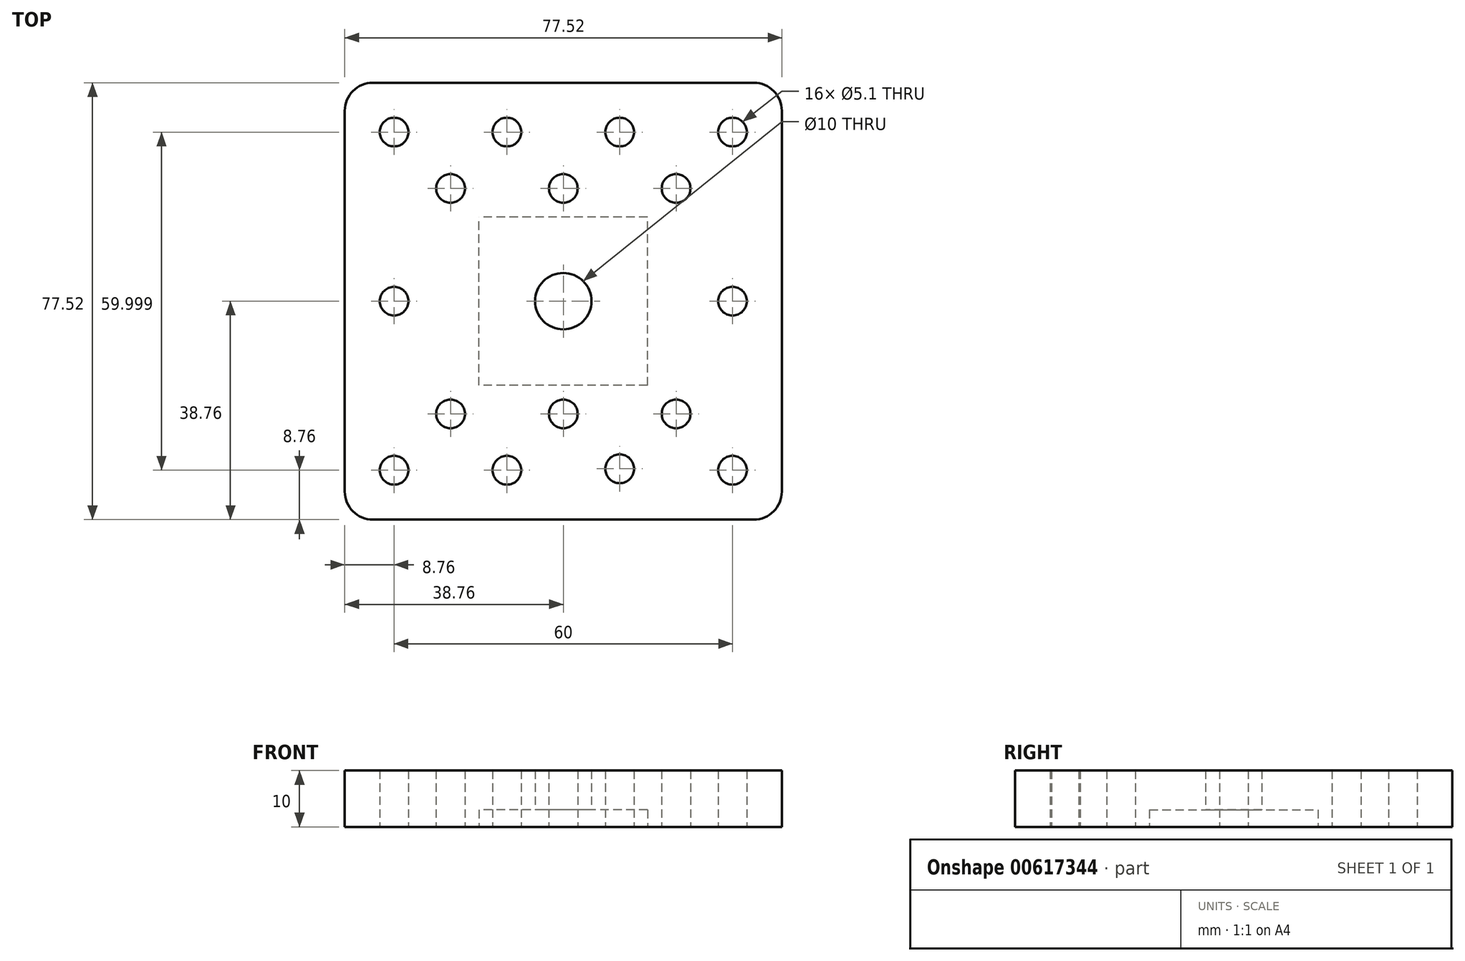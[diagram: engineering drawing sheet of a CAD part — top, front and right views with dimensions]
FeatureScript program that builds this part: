
annotation { "Feature Type Name" : "Feature", "Feature Type Description" : "" }
export const myFeature = defineFeature(function(context is Context, id is Id, definition is map)
    precondition{}
    {
        {
            var Q0;
            Q0=qCreatedBy(makeId("Top.planeOp"),FACE);
            var sketch = newSketch(context, id + "F0", { "sketchPlane" : qUnion([Q0])});
            skLineSegment(sketch, "E0.bottom", {"start": v(38.75, 38.76) * mm, "end": v(-38.76, 38.76) * mm});
            skLineSegment(sketch, "E0.top", {"start": v(38.76, -38.76) * mm, "end": v(-38.76, -38.76) * mm});
            skLineSegment(sketch, "E0.left", {"start": v(38.75, 38.76) * mm, "end": v(38.76, -38.76) * mm});
            skLineSegment(sketch, "E0.right", {"start": v(-38.76, 38.76) * mm, "end": v(-38.75, -38.76) * mm});
            skPoint(sketch, "E0.middle", {"position": v(0, 0) * mm});
            skLineSegment(sketch, "E1.bottom", {"start": v(14.95, -14.95) * mm, "end": v(-14.95, -14.95) * mm});
            skLineSegment(sketch, "E1.top", {"start": v(14.95, 14.95) * mm, "end": v(-14.95, 14.95) * mm});
            skLineSegment(sketch, "E1.left", {"start": v(14.95, -14.95) * mm, "end": v(14.95, 14.95) * mm});
            skLineSegment(sketch, "E1.right", {"start": v(-14.95, -14.95) * mm, "end": v(-14.95, 14.95) * mm});
            skCircle(sketch, "E2", {"center": v(-30, -30) * mm, "radius": 2.55 * mm});
            skCircle(sketch, "E3", {"center": v(-10, -30) * mm, "radius": 2.55 * mm});
            skCircle(sketch, "E4", {"center": v(10, -29.75) * mm, "radius": 2.55 * mm});
            skCircle(sketch, "E5", {"center": v(30, -30) * mm, "radius": 2.55 * mm});
            skCircle(sketch, "E6", {"center": v(20, -20) * mm, "radius": 2.55 * mm});
            skCircle(sketch, "E7", {"center": v(0, -20) * mm, "radius": 2.55 * mm});
            skCircle(sketch, "E8", {"center": v(-20, -20) * mm, "radius": 2.55 * mm});
            skCircle(sketch, "E9", {"center": v(-30, 30) * mm, "radius": 2.55 * mm});
            skCircle(sketch, "E10", {"center": v(-10, 30) * mm, "radius": 2.55 * mm});
            skCircle(sketch, "E11", {"center": v(10, 30) * mm, "radius": 2.55 * mm});
            skCircle(sketch, "E12", {"center": v(30, 30) * mm, "radius": 2.55 * mm});
            skCircle(sketch, "E13", {"center": v(0, 20) * mm, "radius": 2.55 * mm});
            skCircle(sketch, "E14", {"center": v(20, 20) * mm, "radius": 2.55 * mm});
            skCircle(sketch, "E15", {"center": v(-20, 20) * mm, "radius": 2.55 * mm});
            skCircle(sketch, "E16", {"center": v(-30, 0) * mm, "radius": 2.55 * mm});
            skCircle(sketch, "E17", {"center": v(30, 0) * mm, "radius": 2.55 * mm});
            skCircle(sketch, "E18", {"center": v(0, 0) * mm, "radius": 5 * mm});
            skSolve(sketch);
        }
        {
            var Q0;
            Q0=makeQuery(id+"F0.imprint","IMPRINT",FACE,{"disambiguationData":[TD([[makeQuery(id+"F0.imprint","IMPRINT",EDGE,{"derivedFrom":sQuery(id+"F0.wireOp",EDGE,"E0.bottom")}),1.0]])]});
            var Q1;
            Q1=makeQuery(id+"F0.imprint","IMPRINT",FACE,{"disambiguationData":[TD([[makeQuery(id+"F0.imprint","IMPRINT",EDGE,{"derivedFrom":sQuery(id+"F0.wireOp",EDGE,"E1.bottom")}),-1.0]])]});
            extrude(context, id + "F1", {"entities" : qUnion([Q0, Q1]), "depth" : 10 * mm, "offsetDistance" : 25 * mm});
        }
        {
            var Q0;
            Q0=makeQuery(id+"F0.imprint","IMPRINT",FACE,{"disambiguationData":[TD([[makeQuery(id+"F0.imprint","IMPRINT",EDGE,{"derivedFrom":sQuery(id+"F0.wireOp",EDGE,"E1.bottom")}),-1.0]])]});
            extrude(context, id + "F2", {"entities" : qUnion([Q0]), "operationType" : NewBodyOperationType.REMOVE, "depth" : 3 * mm, "offsetDistance" : 25 * mm});
        }
        {
            var Q0;
            Q0=makeQuery(id+"F1.opExtrude","SWEPT_EDGE",EDGE,{"disambiguationData":[OSD([sQuery(id+"F0.wireOp",EDGE,"E0.top"),sQuery(id+"F0.wireOp",EDGE,"E0.left")])]});
            var Q1;
            Q1=makeQuery(id+"F1.opExtrude","SWEPT_EDGE",EDGE,{"disambiguationData":[OSD([sQuery(id+"F0.wireOp",EDGE,"E0.top"),sQuery(id+"F0.wireOp",EDGE,"E0.right")])]});
            var Q2;
            Q2=makeQuery(id+"F1.opExtrude","SWEPT_EDGE",EDGE,{"disambiguationData":[OSD([sQuery(id+"F0.wireOp",EDGE,"E0.bottom"),sQuery(id+"F0.wireOp",EDGE,"E0.left")])]});
            var Q3;
            Q3=makeQuery(id+"F1.opExtrude","SWEPT_EDGE",EDGE,{"disambiguationData":[OSD([sQuery(id+"F0.wireOp",EDGE,"E0.bottom"),sQuery(id+"F0.wireOp",EDGE,"E0.right")])]});
            fillet(context, id + "F3", {"entities" : qUnion([Q0, Q1, Q2, Q3]), "radius" : 5 * mm, "tangentPropagation" : true, "allowEdgeOverflow" : false});
        }
    });
